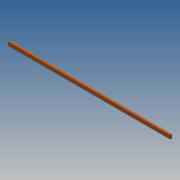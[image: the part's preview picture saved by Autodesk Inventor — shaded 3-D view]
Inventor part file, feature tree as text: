
AUTODESK INVENTOR PART (.ipt)
format: ipt  version: 2013 (Build 170138000, 138)  size: 68,608 bytes
history: native  units: in
note: dims shown in document units (in); Inventor stores cm internally (conversion verified against a paired STEP export)
features: extrude x1, sketch x1
ambient origin geometry x8: Origin, YZ Plane, XZ Plane, XY Plane, X Axis, Y Axis, Z Axis, Center Point
bodies: Solid1 (feature_tree)
feature tree (2):
  extrude  "Extrusion1"  Depth=3.5in
  sketch  "Sketch1"  dims[d0=1.5in d1=3.5in d2=146.5in d3=0.0in]
